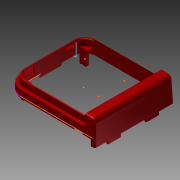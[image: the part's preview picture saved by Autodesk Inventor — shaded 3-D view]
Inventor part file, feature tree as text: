
AUTODESK INVENTOR PART (.ipt)
format: ipt  version: 2013 (Build 170138000, 138)  size: 1,074,688 bytes
history: native  units: in
note: dims shown in document units (in); Inventor stores cm internally (conversion verified against a paired STEP export)
features: sketch x39, extrude x32, reference x10, plane x6, mirror x6, projected_geometry x6, fillet x5, hole x2, loft x1
ambient origin geometry x8: Origin, YZ Plane, XZ Plane, XY Plane, X Axis, Y Axis, Z Axis, Center Point
bodies: Solid1 (feature_tree)
feature tree (107):
  extrude  "Extrusion1"  Depth=0.354in
  fillet  "Fillet1"  Radius=0.064in
  sketch  "Sketch2"  dims[d4=0.064in d9=0.0in d10=90.0deg]
  loft  "Loft2"
  sketch  "Sketch7"  dims[d22=0.0in d23=1.0in d24=0.0in]
  plane  "Work Plane2"
  extrude  "Extrusion2"  Depth=1.0in
  plane  "Work Plane3"
  extrude  "Extrusion4"  Depth=1.0in TaperAngle=0.0deg
  extrude  "Extrusion5"  Depth=0.538in
  extrude  "Extrusion6"  Depth=0.157in TaperAngle=0.0deg
  fillet  "Fillet2"  Radius=0.02in
  extrude  "Extrusion7"  Depth=0.047in
  extrude  "Extrusion9"  Depth=0.168in
  hole  "Hole2"  [1 undecoded]
  plane  "Work Plane4"
  mirror  "Mirror1"
  extrude  "Extrusion10"  Depth=0.303in TaperAngle=0.0deg
  extrude  "Extrusion11"  Depth=0.2771in
  extrude  "Extrusion12"  Depth=0.013in
  extrude  "Extrusion13"  Depth=1.0in TaperAngle=0.0deg
  mirror  "Mirror2"
  sketch  "Sketch24"  dims[d82=0.007in d85=0.079in d86=0.0in d97=0.046in]
  extrude  "Extrusion15"  Depth=0.079in TaperAngle=0.0deg
  sketch  "Sketch26"  dims[d98=0.039in d99=0.0in]
  plane  "Work Plane5"
  sketch  "Sketch27"  dims[d100=0.035in d101=0.193in d102=0.0in]
  fillet  "Fillet3"  Radius=0.046in
  plane  "Work Plane6"
  extrude  "Extrusion17"  TaperAngle=0.0deg  [1 undecoded]
  mirror  "Mirror3"
  extrude  "Extrusion19"  Depth=0.193in TaperAngle=0.0deg
  extrude  "Extrusion20"  Depth=0.461in
  hole  "Hole3"  [1 undecoded]
  extrude  "Extrusion21"  Depth=0.044in
  extrude  "Extrusion22"  Depth=0.059in
  extrude  "Extrusion23"  Depth=0.461in TaperAngle=0.0deg
  mirror  "Mirror4"
  plane  "Work Plane7"
  extrude  "Extrusion24"  Depth=0.461in TaperAngle=0.0deg
  mirror  "Mirror5"
  extrude  "Extrusion25"  Depth=0.098in TaperAngle=0.0deg
  fillet  "Fillet4"  Radius=0.008in
  extrude  "Extrusion27"  Depth=0.217in
  fillet  "Fillet6"  Radius=1.0in
  mirror  "Mirror6"
  extrude  "Extrusion30"  Depth=0.059in TaperAngle=0.0deg
  sketch  "Sketch40"  dims[d166=0.078in d167=0.0in d168=0.62in]
  extrude  "Extrusion31"  Depth=1.0in TaperAngle=0.0deg
  sketch  "Sketch42"  dims[d172=0.01in d173=0.0in d174=0.01in d175=0.0in]
  extrude  "Extrusion32"  Depth=0.078in TaperAngle=0.0deg
  extrude  "Extrusion33"  Depth=0.62in
  sketch  "Sketch43"
  sketch  "Sketch44"
  extrude  "Extrusion34"  Depth=0.078in TaperAngle=0.0deg
  extrude  "Extrusion35"  Depth=0.01in TaperAngle=0.0deg
  sketch  "Sketch47"
  extrude  "Extrusion37"  [1 undecoded]
  extrude  "Extrusion38"  [1 undecoded]
  extrude  "Extrusion39"  [1 undecoded]
  extrude  "Extrusion40"  [1 undecoded]
  extrude  "Extrusion41"  [1 undecoded]
  sketch  "Sketch1"  dims[d0=0.138in d1=-0.0137in d2=0.354in d3=0.064in]
  sketch  "Sketch3"  dims[d11=0.0in d12=90.0deg d18=1.0in d19=0.0137in]
  sketch  "Sketch9"  dims[d25=1.0in d26=0.0in d27=0.538in d28=0.4198in]
  reference  "Reference5"
  sketch  "Sketch10"  dims[d29=0.354in d30=0.157in d31=0.0in d32=0.02in]
  projected_geometry  "Projected Loop4"
  sketch  "Sketch11"  dims[d33=0.157in d34=0.0in d49=0.047in]
  sketch  "Sketch12"  dims[d50=0.079in d51=0.168in]
  sketch  "Sketch15"  dims[d52=0.225in d53=-0.0034in]
  reference  "Reference7"
  reference  "Reference8"
  reference  "Reference9"
  sketch  "Sketch16"  dims[d54=0.067in d55=0.75in d56=0.106in d57=0.25in d58=0.5635in d59=0.25in d60=0.8108in d61=0.281in]
  sketch  "Sketch17"  dims[d62=0.223in d63=0.303in d64=0.0in]
  sketch  "Sketch19"  dims[d65=0.281in d71=0.2771in]
  reference  "Reference10"
  sketch  "Sketch21"  dims[d73=0.079in d74=0.0in d77=0.013in]
  sketch  "Sketch22"  dims[d78=0.079in d79=0.0in d80=1.0in d81=0.0in]
  sketch  "Sketch28"  dims[d105=0.182in d106=0.0in d108=0.461in d109=-0.0034in]
  sketch  "Sketch29"  dims[d110=0.066in d111=0.75in d112=0.106in d113=0.25in d114=135.0deg d115=1.0in d116=0.0in d117=0.6219in]
  sketch  "Sketch30"  dims[d118=0.461in d119=0.0in d120=0.044in]
  reference  "Reference11"
  sketch  "Sketch31"  dims[d121=0.461in d122=0.0in d123=0.059in]
  sketch  "Sketch32"  dims[d124=0.461in d125=0.0in d126=0.461in d127=0.0in]
  sketch  "Sketch33"  dims[d128=0.059in d129=0.461in d130=0.0in]
  sketch  "Sketch34"  dims[d131=0.059in d134=0.098in d135=0.0in d137=0.008in]
  sketch  "Sketch35"  dims[d146=1.0in d147=0.0in d148=0.217in d149=1.0in d150=0.0in]
  sketch  "Sketch36"  dims[d151=0.079in d152=0.0in d153=0.059in d154=0.0in]
  sketch  "Sketch37"  dims[d155=0.039in d156=1.0in d157=0.0in]
  sketch  "Sketch38"  dims[d158=1.0in d159=0.0in d164=0.078in d165=0.0in]
  reference  "Reference12"
  reference  "Reference13"
  reference  "Reference14"
  reference  "Reference15"
  sketch  "Sketch41"  dims[d169=0.047in d170=0.078in d171=0.0in]
  projected_geometry  "Projected Loop7"
  sketch  "Sketch45"
  sketch  "Sketch46"
  sketch  "Sketch48"
  sketch  "Sketch49"
  sketch  "Sketch50"
  projected_geometry  "Project Cut Edges2"
  projected_geometry  "Project Cut Edges3"
  projected_geometry  "Project Cut Edges4"
  projected_geometry  "Project Cut Edges5"
note: 8 required parameter values undecoded (feature->parameter linkage not recoverable at this tier; creation-order binding heuristic only, values carry confidence <= 0.55)
